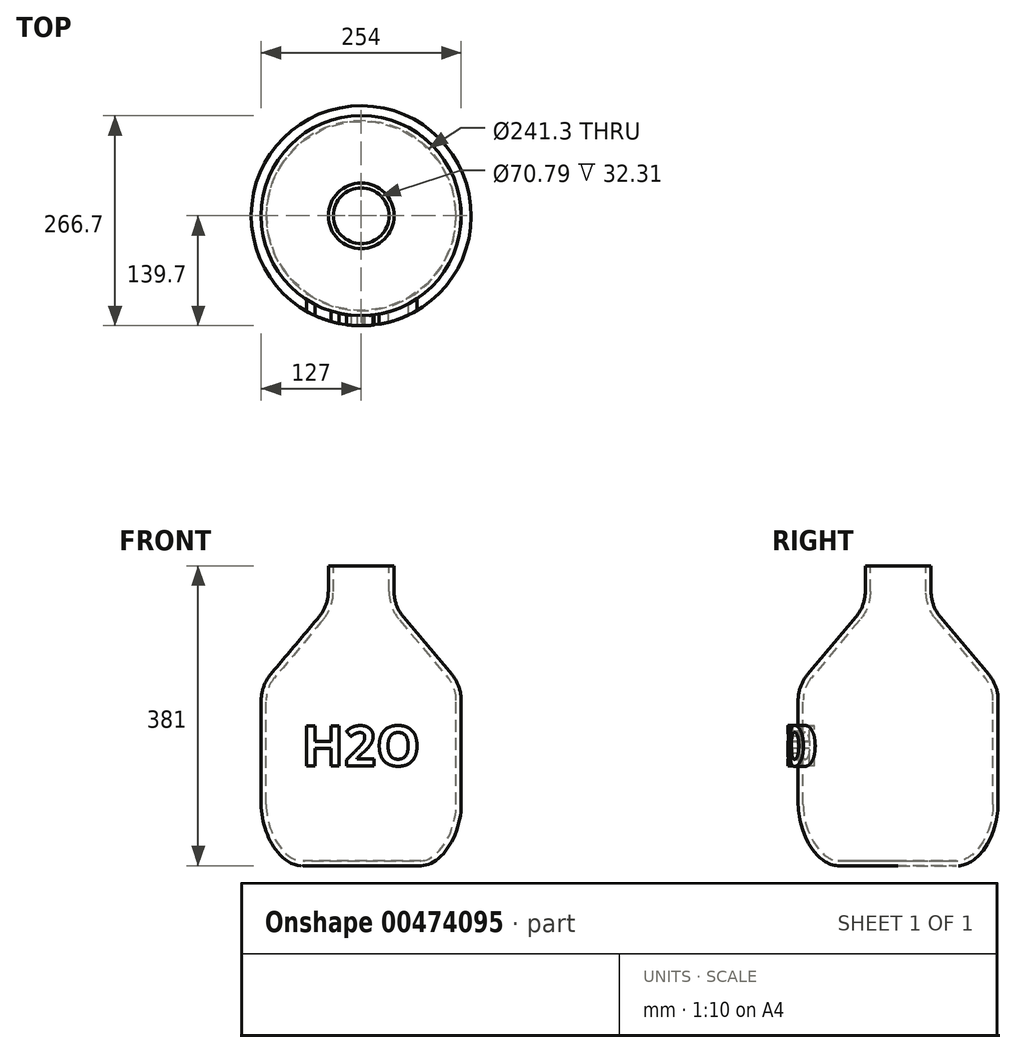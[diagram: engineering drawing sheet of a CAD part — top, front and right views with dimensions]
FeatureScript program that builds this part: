
annotation { "Feature Type Name" : "Feature", "Feature Type Description" : "" }
export const myFeature = defineFeature(function(context is Context, id is Id, definition is map)
    precondition{}
    {
        {
            var Q0;
            Q0=qCreatedBy(makeId("Front.planeOp"),FACE);
            var sketch = newSketch(context, id + "F0", { "sketchPlane" : qUnion([Q0])});
            skLineSegment(sketch, "E0", {"start": v(0, 0) * mm, "end": v(76.2, 0) * mm});
            skLineSegment(sketch, "E1", {"start": v(127, 78.2) * mm, "end": v(127, 228.6) * mm});
            skLineSegment(sketch, "E2", {"start": v(127, 228.6) * mm, "end": v(41.75, 330.2) * mm});
            skLineSegment(sketch, "E3", {"start": v(41.75, 330.2) * mm, "end": v(41.75, 381) * mm});
            skEllipticalArc(sketch, "E4", {});
            skPoint(sketch, "E5", {"position": v(76.2, 0) * mm});
            skPoint(sketch, "E6", {"position": v(127, 78.2) * mm});
            skLineSegment(sketch, "E7", {"start": v(0, 381) * mm, "end": v(41.75, 381) * mm});
            skLineSegment(sketch, "E8", {"start": v(0, 381) * mm, "end": v(0, 0) * mm});
            const initialGuessF0  = {"E4": [0.08666226350505683, 0.0621025523989516, 0.26079741740588636, 0.9653935503588265, 0.0635, 0.0381, 3.302282869680676, 5.135445547670018]};
            skSetInitialGuess(sketch, initialGuessF0);
            skSolve(sketch);
        }
        {
            var Q0;
            Q0=makeQuery(id+"F0.imprint","IMPRINT",FACE,{"disambiguationData":[TD([[makeQuery(id+"F0.imprint","IMPRINT",EDGE,{"derivedFrom":sQuery(id+"F0.wireOp",EDGE,"E0")}),1.0]])]});
            var Q1;
            Q1=sQuery(id+"F0.wireOp",EDGE,"E8");
            revolve(context, id + "F1", {"entities" : qUnion([Q0]), "axis" : qUnion([Q1]), "revolveType" : RevolveType.FULL});
        }
        {
            var Q0;
            Q0=makeQuery(id+"F1.opRevolve","SWEPT_EDGE",EDGE,{"disambiguationData":[OSD([sQuery(id+"F0.wireOp",EDGE,"E2"),sQuery(id+"F0.wireOp",EDGE,"E3")])]});
            var Q1;
            Q1=makeQuery(id+"F1.opRevolve","SWEPT_EDGE",EDGE,{"disambiguationData":[OSD([sQuery(id+"F0.wireOp",EDGE,"E1"),sQuery(id+"F0.wireOp",EDGE,"E2")])]});
            fillet(context, id + "F2", {"entities" : qUnion([Q0, Q1]), "radius" : 50.8 * mm, "tangentPropagation" : true, "allowEdgeOverflow" : false});
        }
        {
            var Q0;
            Q0=makeQuery(id+"F1.opRevolve","SWEPT_FACE",FACE,{"disambiguationData":[OSD([sQuery(id+"F0.wireOp",EDGE,"E7")])]});
            shell(context, id + "F3", {"entities" : qUnion([Q0]), "thickness" : 6.35 * mm});
        }
        {
            var Q0;
            Q0=qCreatedBy(makeId("Front.planeOp"),FACE);
            cPlane(context, id + "F4", {"entities" : qUnion([Q0]), "cplaneType" : CPlaneType.OFFSET, "offset" : 139.7 * mm, "width" : 152.4 * mm, "height" : 152.4 * mm});
        }
        {
            var Q0;
            Q0=qCreatedBy(id+"F4.planeOp",FACE);
            var sketch = newSketch(context, id + "F5", { "sketchPlane" : qUnion([Q0])});
            skText(sketch, "E9", { "text": "H2O", "fontName": "OpenSans-Bold.ttf"});
            const initialGuessF5  = {"E9": [-0.07544, 0.127, 1, 0, 0.0508]};
            skSetInitialGuess(sketch, initialGuessF5);
            skSolve(sketch);
        }
        {
            var Q0;
            Q0 = qSketchRegion(id + "F5", true);
            var Q1;
            Q1=makeQuery(id+"F1.opRevolve","SWEPT_FACE",FACE,{"disambiguationData":[OSD([sQuery(id+"F0.wireOp",EDGE,"E1")])]});
            extrude(context, id + "F6", {"entities" : qUnion([Q0]), "operationType" : NewBodyOperationType.ADD, "endBound" : BoundingType.UP_TO_SURFACE, "oppositeDirection" : true, "endBoundEntityFace" : qUnion([Q1]), "depth" : 25.4 * mm});
        }
        {
            var Q0;
            Q0=qCreatedBy(makeId("Top.planeOp"),FACE);
            var sketch = newSketch(context, id + "F7", { "sketchPlane" : qUnion([Q0])});
            skCircle(sketch, "E10", {"center": v(0, 0) * mm, "radius": 139.7 * mm});
            skSolve(sketch);
        }
        {
            var Q0;
            Q0=makeQuery(id+"F7.imprint","IMPRINT",FACE,{"disambiguationData":[TD([[makeQuery(id+"F7.imprint","IMPRINT",EDGE,{"derivedFrom":sQuery(id+"F7.wireOp",EDGE,"E10")}),1.0]])]});
            extrude(context, id + "F8", {"entities" : qUnion([Q0]), "operationType" : NewBodyOperationType.INTERSECT, "endBound" : BoundingType.THROUGH_ALL, "depth" : 25.4 * mm});
        }
    });
